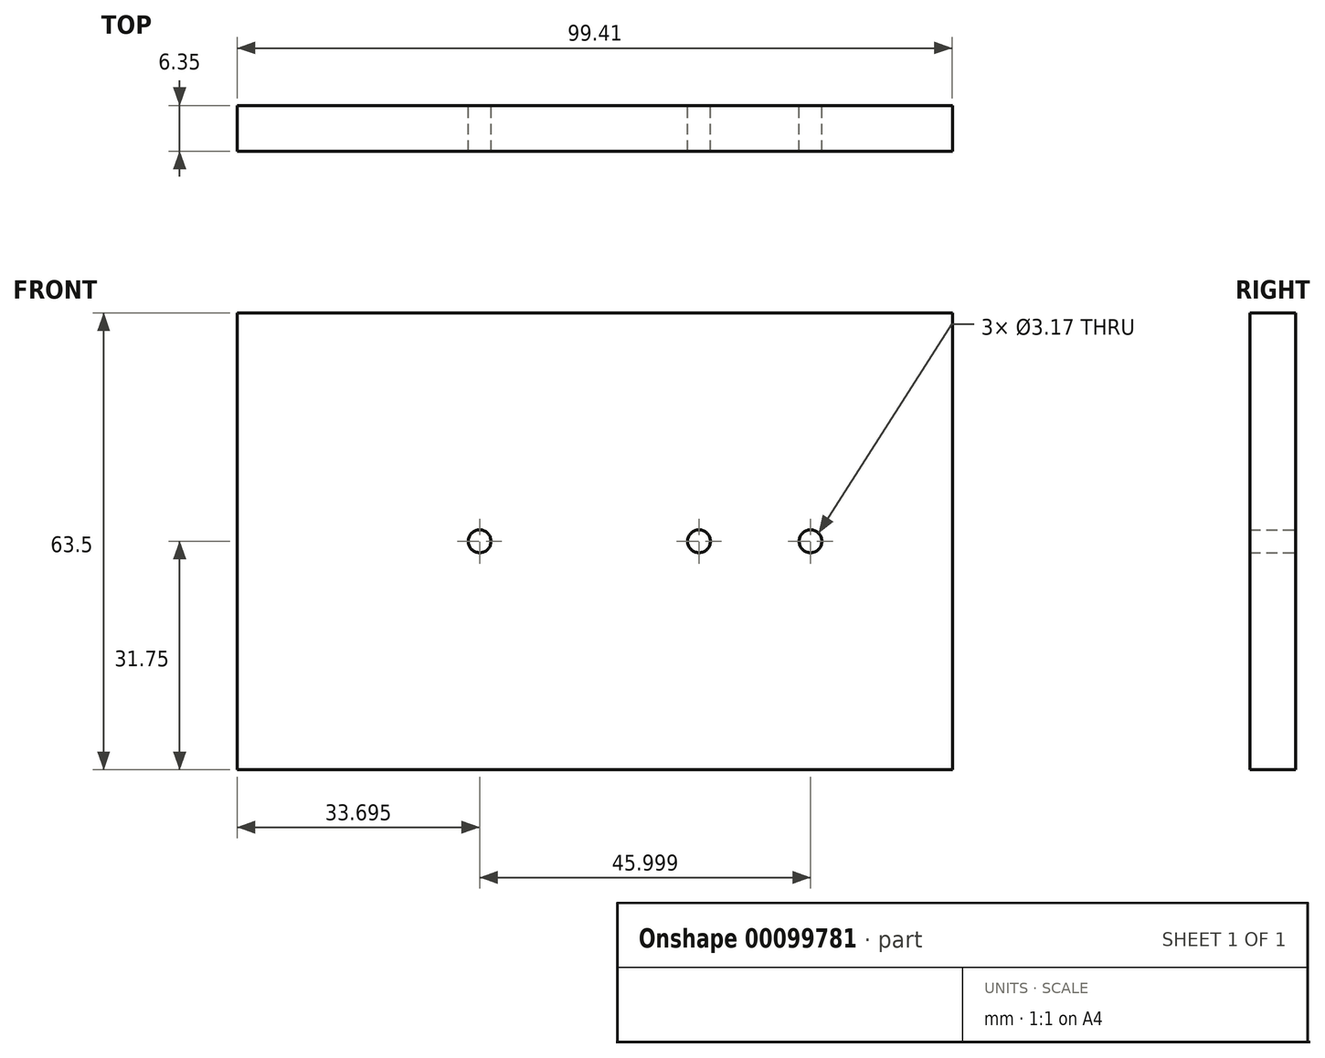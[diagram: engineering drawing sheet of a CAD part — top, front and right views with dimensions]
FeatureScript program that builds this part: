
annotation { "Feature Type Name" : "Feature", "Feature Type Description" : "" }
export const myFeature = defineFeature(function(context is Context, id is Id, definition is map)
    precondition{}
    {
        {
            var Q0;
            Q0=qCreatedBy(makeId("Front.planeOp"),FACE);
            var sketch = newSketch(context, id + "F0", { "sketchPlane" : qUnion([Q0])});
            skPoint(sketch, "E0", {"position": v(-34.4, 0) * mm});
            skPoint(sketch, "E1", {"position": v(-3.9, 0) * mm});
            skLineSegment(sketch, "E2", {"start": v(-68.1, 0) * mm, "end": v(-68.1, 31.75) * mm});
            skLineSegment(sketch, "E3.bottom", {"start": v(-68.1, 31.75) * mm, "end": v(31.32, 31.75) * mm});
            skLineSegment(sketch, "E3.top", {"start": v(-68.1, -31.75) * mm, "end": v(31.32, -31.75) * mm});
            skLineSegment(sketch, "E3.left", {"start": v(-68.1, 31.75) * mm, "end": v(-68.1, -31.75) * mm});
            skLineSegment(sketch, "E3.right", {"start": v(31.32, 31.75) * mm, "end": v(31.32, -31.75) * mm});
            skCircle(sketch, "E4", {"center": v(-34.4, 0) * mm, "radius": 1.59 * mm});
            skCircle(sketch, "E5", {"center": v(11.6, 0) * mm, "radius": 1.59 * mm});
            skCircle(sketch, "E6", {"center": v(-3.9, 0) * mm, "radius": 1.59 * mm});
            skSolve(sketch);
        }
        {
            var Q0;
            {var subQ1=sQuery(id+"F0.wireOp",EDGE,"E3.bottom");Q0=makeQuery(id+"F0.imprint","IMPRINT",FACE,{"disambiguationData":[TD([[makeQuery(id+"F0.imprint","IMPRINT",EDGE,{"derivedFrom":subQ1}),-1.0]])]});}
            extrude(context, id + "F1", {"entities" : qUnion([Q0]), "depth" : 6.35 * mm});
        }
    });
